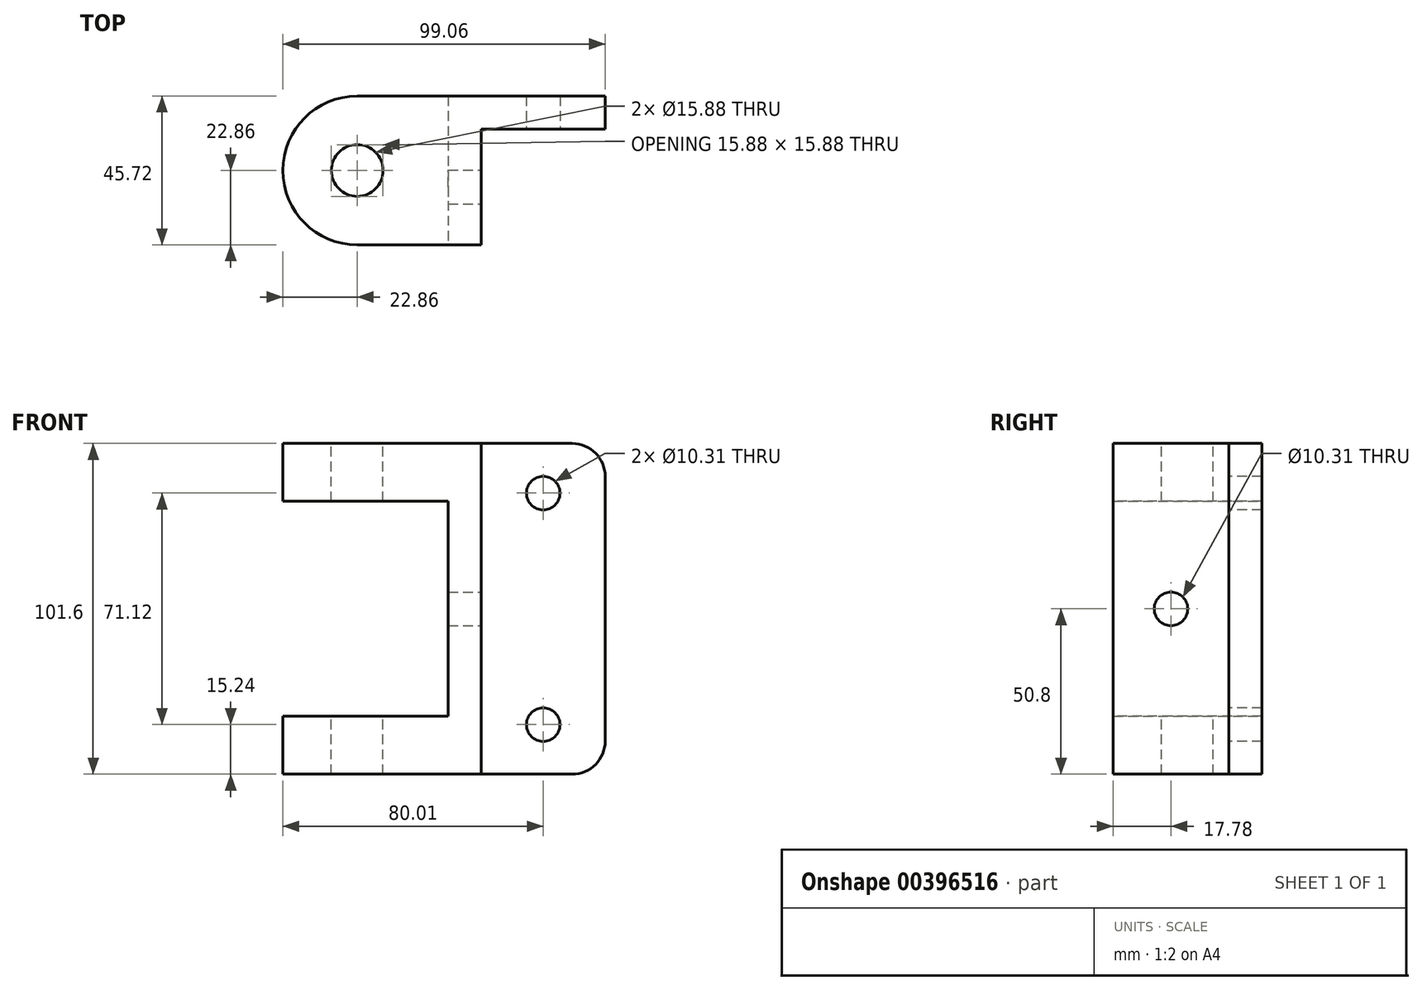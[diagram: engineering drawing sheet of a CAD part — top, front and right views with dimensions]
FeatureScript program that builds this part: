
annotation { "Feature Type Name" : "Feature", "Feature Type Description" : "" }
export const myFeature = defineFeature(function(context is Context, id is Id, definition is map)
    precondition{}
    {
        {
            var Q0;
            Q0=qCreatedBy(makeId("Front.planeOp"),FACE);
            var sketch = newSketch(context, id + "F0", { "sketchPlane" : qUnion([Q0])});
            skLineSegment(sketch, "E0.bottom", {"start": v(0, 0) * mm, "end": v(99.06, 0) * mm});
            skLineSegment(sketch, "E0.top", {"start": v(0, 101.6) * mm, "end": v(99.06, 101.6) * mm});
            skLineSegment(sketch, "E0.left", {"start": v(0, 0) * mm, "end": v(0, 101.6) * mm});
            skLineSegment(sketch, "E0.right", {"start": v(99.06, 0) * mm, "end": v(99.06, 101.6) * mm});
            skSolve(sketch);
        }
        {
            var Q0;
            Q0=makeQuery(id+"F0.imprint","IMPRINT",FACE,{"disambiguationData":[TD([[makeQuery(id+"F0.imprint","IMPRINT",EDGE,{"derivedFrom":sQuery(id+"F0.wireOp",EDGE,"E0.bottom")}),1.0]])]});
            extrude(context, id + "F1", {"entities" : qUnion([Q0]), "depth" : 45.72 * mm});
        }
        {
            var Q0;
            Q0=makeQuery(id+"F1.opExtrude","CAP_FACE",FACE,{"disambiguationData":[OSD([sQuery(id+"F0.wireOp",EDGE,"E0.bottom"),sQuery(id+"F0.wireOp",EDGE,"E0.top"),sQuery(id+"F0.wireOp",EDGE,"E0.left"),sQuery(id+"F0.wireOp",EDGE,"E0.right")])],"isStart":false});
            var sketch = newSketch(context, id + "F2", { "sketchPlane" : qUnion([Q0])});
            skLineSegment(sketch, "E1.bottom", {"start": v(99.06, 101.6) * mm, "end": v(60.96, 101.6) * mm});
            skLineSegment(sketch, "E1.top", {"start": v(99.06, 0) * mm, "end": v(60.96, 0) * mm});
            skLineSegment(sketch, "E1.left", {"start": v(99.06, 101.6) * mm, "end": v(99.06, 0) * mm});
            skLineSegment(sketch, "E1.right", {"start": v(60.96, 101.6) * mm, "end": v(60.96, 0) * mm});
            skSolve(sketch);
        }
        {
            var Q0;
            Q0=makeQuery(id+"F2.imprint","IMPRINT",FACE,{"disambiguationData":[TD([[makeQuery(id+"F2.imprint","IMPRINT",EDGE,{"derivedFrom":sQuery(id+"F2.wireOp",EDGE,"E1.bottom")}),-1.0]])]});
            extrude(context, id + "F3", {"entities" : qUnion([Q0]), "operationType" : NewBodyOperationType.REMOVE, "oppositeDirection" : true, "depth" : 35.56 * mm});
        }
        {
            var Q0;
            Q0=makeQuery(id+"F1.opExtrude","SWEPT_FACE",FACE,{"disambiguationData":[OSD([sQuery(id+"F0.wireOp",EDGE,"E0.left")])]});
            var sketch = newSketch(context, id + "F4", { "sketchPlane" : qUnion([Q0])});
            skLineSegment(sketch, "E2", {"start": v(0, 101.6) * mm, "end": v(0, 83.82) * mm});
            skLineSegment(sketch, "E3", {"start": v(0, 0) * mm, "end": v(0, 17.78) * mm});
            skLineSegment(sketch, "E4.bottom", {"start": v(0, 83.82) * mm, "end": v(45.72, 83.82) * mm});
            skLineSegment(sketch, "E4.top", {"start": v(0, 17.78) * mm, "end": v(45.72, 17.78) * mm});
            skLineSegment(sketch, "E4.left", {"start": v(0, 83.82) * mm, "end": v(0, 17.78) * mm});
            skLineSegment(sketch, "E4.right", {"start": v(45.72, 83.82) * mm, "end": v(45.72, 17.78) * mm});
            skSolve(sketch);
        }
        {
            var Q0;
            Q0=makeQuery(id+"F4.imprint","IMPRINT",FACE,{"disambiguationData":[TD([[makeQuery(id+"F4.imprint","IMPRINT",EDGE,{"derivedFrom":sQuery(id+"F4.wireOp",EDGE,"E4.bottom")}),-1.0]])]});
            extrude(context, id + "F5", {"entities" : qUnion([Q0]), "operationType" : NewBodyOperationType.REMOVE, "oppositeDirection" : true, "depth" : 50.8 * mm});
        }
        {
            var Q0;
            Q0=makeQuery(id+"F1.opExtrude","SWEPT_FACE",FACE,{"disambiguationData":[OSD([sQuery(id+"F0.wireOp",EDGE,"E0.top")])]});
            var sketch = newSketch(context, id + "F6", { "sketchPlane" : qUnion([Q0])});
            skCircle(sketch, "E5", {"center": v(22.86, -22.86) * mm, "radius": 7.94 * mm});
            skPoint(sketch, "E5.centerSnap0", {"position": v(0, -22.86) * mm});
            skCircle(sketch, "E6", {"center": v(22.86, -22.86) * mm, "radius": 22.86 * mm});
            skSolve(sketch);
        }
        {
            var Q0;
            Q0=makeQuery(id+"F6.imprint","IMPRINT",FACE,{"disambiguationData":[TD([[makeQuery(id+"F6.imprint","IMPRINT",EDGE,{"derivedFrom":sQuery(id+"F6.wireOp",EDGE,"E5")}),1.0]])]});
            var Q1;
            {var subQ0=sQuery(id+"F6.wireOp",EDGE,"E6");var subQ1=sQuery(id+"F0.wireOp",EDGE,"E0.top");var subQ4=makeQuery(id+"F1.opExtrude","CAP_EDGE",EDGE,{"disambiguationData":[OSD([subQ1])],"isStart":true});var subQ5=makeQuery(id+"F6.imprint","INTERSECT",VERTEX,{"derivedFrom":[subQ4,subQ0]});Q1=makeQuery(id+"F6.imprint","IMPRINT",FACE,{"disambiguationData":[TD([[makeQuery(id+"F6.imprint","IMPRINT",EDGE,{"disambiguationData":[TD([[subQ5,-1.0]])],"derivedFrom":subQ0}),-1.0]])]});}
            var Q2;
            {var subQ0=sQuery(id+"F6.wireOp",EDGE,"E6");var subQ1=sQuery(id+"F0.wireOp",EDGE,"E0.top");var subQ4=makeQuery(id+"F1.opExtrude","CAP_EDGE",EDGE,{"disambiguationData":[OSD([subQ1])],"isStart":false});var subQ5=makeQuery(id+"F6.imprint","INTERSECT",VERTEX,{"derivedFrom":[subQ4,subQ0]});Q2=makeQuery(id+"F6.imprint","IMPRINT",FACE,{"disambiguationData":[TD([[makeQuery(id+"F6.imprint","IMPRINT",EDGE,{"disambiguationData":[TD([[subQ5,1.0]])],"derivedFrom":subQ0}),-1.0]])]});}
            extrude(context, id + "F7", {"entities" : qUnion([Q0, Q1, Q2]), "operationType" : NewBodyOperationType.REMOVE, "endBound" : BoundingType.THROUGH_ALL, "oppositeDirection" : true, "depth" : 25.4 * mm});
        }
        {
            var Q0;
            Q0=makeQuery(id+"F3.boolean.opBoolean","COPY",FACE,{"derivedFrom":makeQuery(id+"F3.opExtrude","SWEPT_FACE",FACE,{"disambiguationData":[OSD([sQuery(id+"F2.wireOp",EDGE,"E1.right")])]})});
            var sketch = newSketch(context, id + "F8", { "sketchPlane" : qUnion([Q0])});
            skCircle(sketch, "E7", {"center": v(-27.94, 50.8) * mm, "radius": 5.16 * mm});
            skPoint(sketch, "E7.centerSnap0", {"position": v(-27.94, 0) * mm});
            skSolve(sketch);
        }
        {
            var Q0;
            Q0=makeQuery(id+"F8.imprint","IMPRINT",FACE,{"disambiguationData":[TD([[makeQuery(id+"F8.imprint","IMPRINT",EDGE,{"derivedFrom":sQuery(id+"F8.wireOp",EDGE,"E7")}),1.0]])]});
            extrude(context, id + "F9", {"entities" : qUnion([Q0]), "operationType" : NewBodyOperationType.REMOVE, "endBound" : BoundingType.THROUGH_ALL, "oppositeDirection" : true, "depth" : 25.4 * mm});
        }
        {
            var Q0;
            Q0=makeQuery(id+"F3.boolean.opBoolean","COPY",FACE,{"derivedFrom":makeQuery(id+"F3.opExtrude","CAP_FACE",FACE,{"disambiguationData":[OSD([sQuery(id+"F2.wireOp",EDGE,"E1.bottom"),sQuery(id+"F2.wireOp",EDGE,"E1.top"),sQuery(id+"F2.wireOp",EDGE,"E1.left"),sQuery(id+"F2.wireOp",EDGE,"E1.right")])],"isStart":false})});
            var sketch = newSketch(context, id + "F10", { "sketchPlane" : qUnion([Q0])});
            skCircle(sketch, "E8", {"center": v(80, 86.36) * mm, "radius": 5.16 * mm});
            skPoint(sketch, "E8.centerSnap0", {"position": v(80, 101.6) * mm});
            skCircle(sketch, "E9", {"center": v(80.01, 15.24) * mm, "radius": 5.16 * mm});
            skPoint(sketch, "E9.centerSnap0", {"position": v(80.01, 0) * mm});
            skSolve(sketch);
        }
        {
            var Q0;
            Q0=makeQuery(id+"F10.imprint","IMPRINT",FACE,{"disambiguationData":[TD([[makeQuery(id+"F10.imprint","IMPRINT",EDGE,{"derivedFrom":sQuery(id+"F10.wireOp",EDGE,"E8")}),1.0]])]});
            var Q1;
            Q1=makeQuery(id+"F10.imprint","IMPRINT",FACE,{"disambiguationData":[TD([[makeQuery(id+"F10.imprint","IMPRINT",EDGE,{"derivedFrom":sQuery(id+"F10.wireOp",EDGE,"E9")}),1.0]])]});
            extrude(context, id + "F11", {"entities" : qUnion([Q0, Q1]), "operationType" : NewBodyOperationType.REMOVE, "endBound" : BoundingType.THROUGH_ALL, "oppositeDirection" : true, "depth" : 25.4 * mm});
        }
        {
            var Q0;
            Q0=makeQuery(id+"F1.opExtrude","SWEPT_EDGE",EDGE,{"disambiguationData":[OSD([sQuery(id+"F0.wireOp",EDGE,"E0.top"),sQuery(id+"F0.wireOp",EDGE,"E0.right")])]});
            var Q1;
            Q1=makeQuery(id+"F1.opExtrude","SWEPT_EDGE",EDGE,{"disambiguationData":[OSD([sQuery(id+"F0.wireOp",EDGE,"E0.bottom"),sQuery(id+"F0.wireOp",EDGE,"E0.right")])]});
            fillet(context, id + "F12", {"entities" : qUnion([Q0, Q1]), "radius" : 10.16 * mm, "tangentPropagation" : true, "allowEdgeOverflow" : false});
        }
    });
